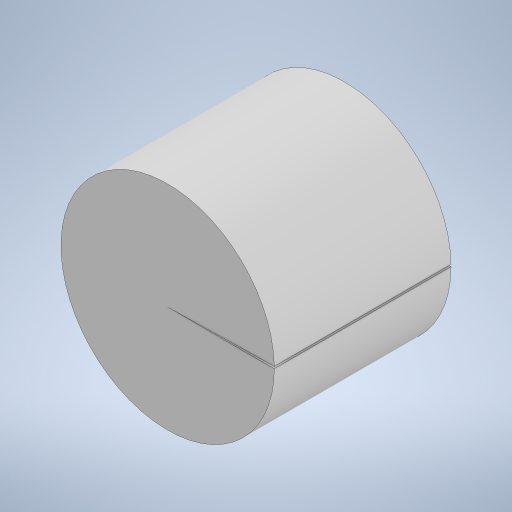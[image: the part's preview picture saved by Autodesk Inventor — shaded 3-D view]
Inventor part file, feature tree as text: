
AUTODESK INVENTOR PART (.ipt)
format: ipt  version: 2024 (Build 280153000, 153)  size: 231,424 bytes
history: native  units: mm
features: extrude x1, sketch x1
ambient origin geometry x8: Origin, YZ Plane, XZ Plane, XY Plane, X Axis, Y Axis, Z Axis, Center Point
bodies: Solid1 (feature_tree)
feature tree (2):
  extrude  "Extrusion1"  Depth=6.0mm
  sketch  "Sketch1"  dims[d0=2.184152mm d1=7.244286mm d2=62.65732mm d3=6.0mm d4=0.0mm]
